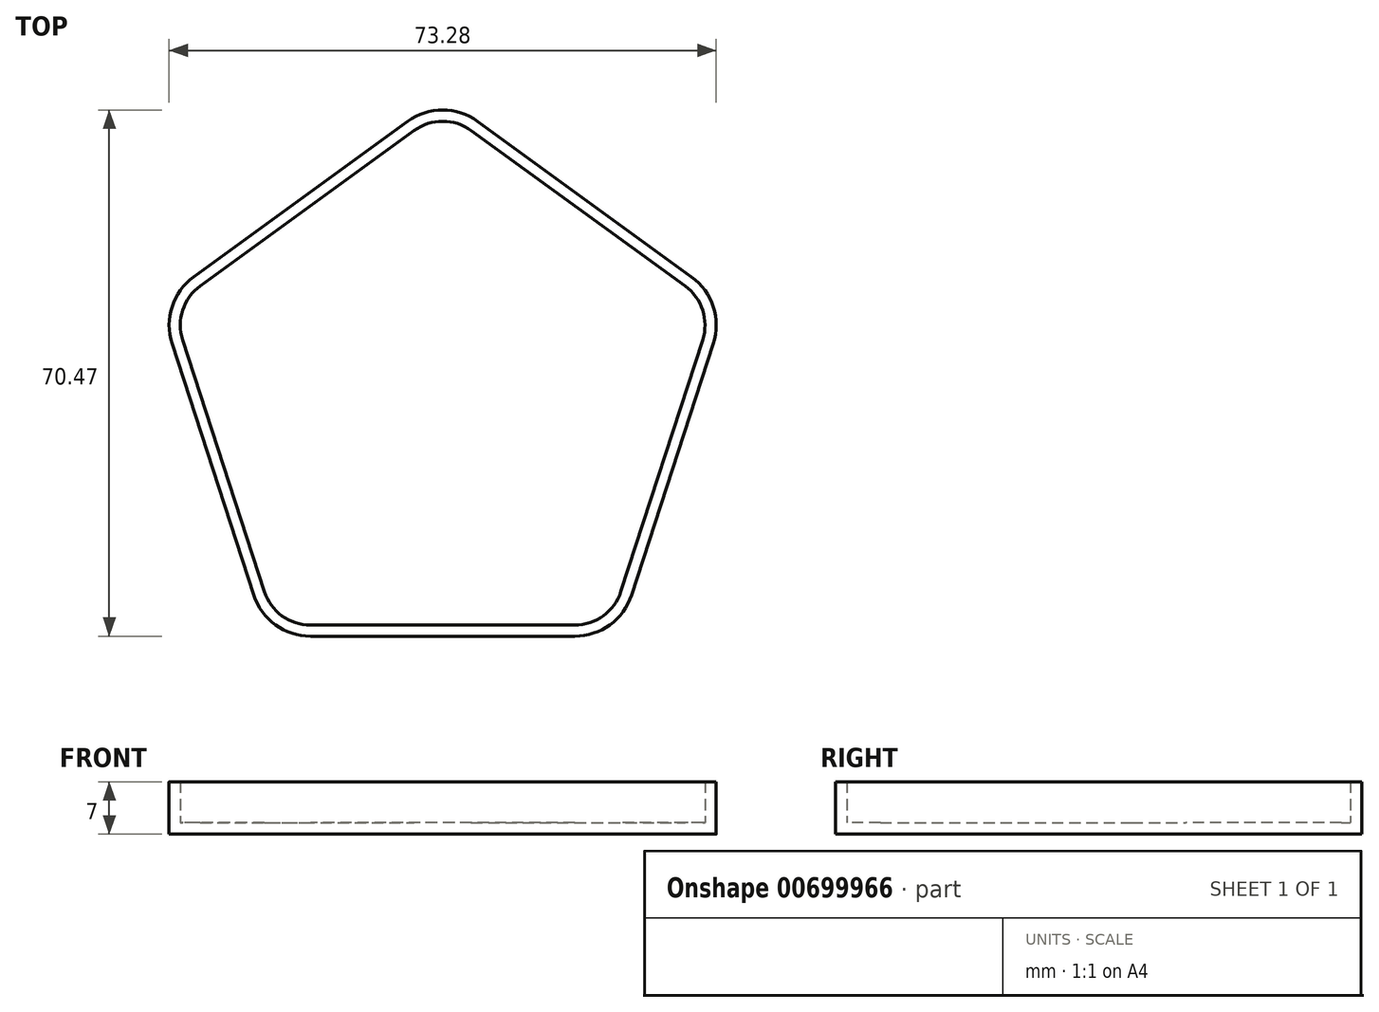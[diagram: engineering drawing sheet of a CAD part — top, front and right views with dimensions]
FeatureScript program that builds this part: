
annotation { "Feature Type Name" : "Feature", "Feature Type Description" : "" }
export const myFeature = defineFeature(function(context is Context, id is Id, definition is map)
    precondition{}
    {
        {
            assignVariable(context, id + "F0", {"name" : "thickness", "anyValue" : 1.5 * mm});
        }
        {
            assignVariable(context, id + "F1", {"name" : "half_height", "anyValue" : 7 * mm});
        }
        {
            var Q0;
            Q0=qCreatedBy(makeId("Top.planeOp"),FACE);
            var sketch = newSketch(context, id + "F2", { "sketchPlane" : qUnion([Q0])});
            skCircle(sketch, "E0.cCircle", {"center": v(0, 0) * mm, "radius": 40 * mm, "construction": true});
            skLineSegment(sketch, "E0.0", {"start": v(36.25, 6.83) * mm, "end": v(25.3, -26.83) * mm});
            skLineSegment(sketch, "E0.1", {"start": v(17.7, -32.36) * mm, "end": v(-17.7, -32.36) * mm});
            skLineSegment(sketch, "E0.2", {"start": v(-25.3, -26.83) * mm, "end": v(-36.25, 6.83) * mm});
            skLineSegment(sketch, "E0.3", {"start": v(-33.34, 15.78) * mm, "end": v(-4.7, 36.58) * mm});
            skLineSegment(sketch, "E0.4", {"start": v(4.7, 36.58) * mm, "end": v(33.34, 15.78) * mm});
            skLineSegment(sketch, "E1", {"start": v(-38.04, 12.36) * mm, "end": v(38.04, 12.36) * mm, "construction": true});
            skLineSegment(sketch, "E2", {"start": v(0, 40) * mm, "end": v(0, -32.36) * mm, "construction": true});
            skPoint(sketch, "E3.visualSharp", {"position": v(0, 40) * mm});
            skArc(sketch, "E3.filletArc", {"start": v(4.7, 36.58) * mm, "mid": v(0, 38.11) * mm, "end": v(-4.7, 36.58) * mm});
            skPoint(sketch, "E4.visualSharp", {"position": v(-38.04, 12.36) * mm});
            skArc(sketch, "E4.filletArc", {"start": v(-33.34, 15.78) * mm, "mid": v(-36.25, 11.78) * mm, "end": v(-36.25, 6.83) * mm});
            skPoint(sketch, "E5.visualSharp", {"position": v(-23.51, -32.36) * mm});
            skArc(sketch, "E5.filletArc", {"start": v(-25.3, -26.83) * mm, "mid": v(-22.4, -30.83) * mm, "end": v(-17.7, -32.36) * mm});
            skPoint(sketch, "E6.visualSharp", {"position": v(23.51, -32.36) * mm});
            skArc(sketch, "E6.filletArc", {"start": v(17.7, -32.36) * mm, "mid": v(22.4, -30.83) * mm, "end": v(25.3, -26.83) * mm});
            skPoint(sketch, "E7.visualSharp", {"position": v(38.04, 12.36) * mm});
            skArc(sketch, "E7.filletArc", {"start": v(36.25, 6.83) * mm, "mid": v(36.25, 11.78) * mm, "end": v(33.34, 15.78) * mm});
            skLineSegment(sketch, "E8", {"start": v(-2, 12.36) * mm, "end": v(-2, -32.36) * mm, "construction": true});
            skPoint(sketch, "E9", {"position": v(-2, -10) * mm});
            skLineSegment(sketch, "E10", {"start": v(30.78, -10) * mm, "end": v(-30.78, -10) * mm, "construction": true});
            skSolve(sketch);
        }
        {
            var Q0;
            Q0=makeQuery(id+"F2.imprint","IMPRINT",FACE,{"disambiguationData":[TD([[makeQuery(id+"F2.imprint","IMPRINT",EDGE,{"derivedFrom":sQuery(id+"F2.wireOp",EDGE,"E0.0")}),-1.0]])]});
            extrude(context, id + "F3", {"entities" : qUnion([Q0]), "depth" : getVariable(context, 'half_height'), "offsetDistance" : 25 * mm});
        }
        {
            var Q0;
            Q0=makeQuery(id+"F3.opExtrude","CAP_FACE",FACE,{"disambiguationData":[OSD([sQuery(id+"F2.wireOp",EDGE,"E0.0"),sQuery(id+"F2.wireOp",EDGE,"E0.1"),sQuery(id+"F2.wireOp",EDGE,"E0.2"),sQuery(id+"F2.wireOp",EDGE,"E0.3"),sQuery(id+"F2.wireOp",EDGE,"E0.4"),sQuery(id+"F2.wireOp",EDGE,"E3.filletArc"),sQuery(id+"F2.wireOp",EDGE,"E4.filletArc"),sQuery(id+"F2.wireOp",EDGE,"E5.filletArc"),sQuery(id+"F2.wireOp",EDGE,"E6.filletArc"),sQuery(id+"F2.wireOp",EDGE,"E7.filletArc")])],"isStart":false});
            shell(context, id + "F4", {"entities" : qUnion([Q0]), "thickness" : getVariable(context, 'thickness')});
        }
    });
